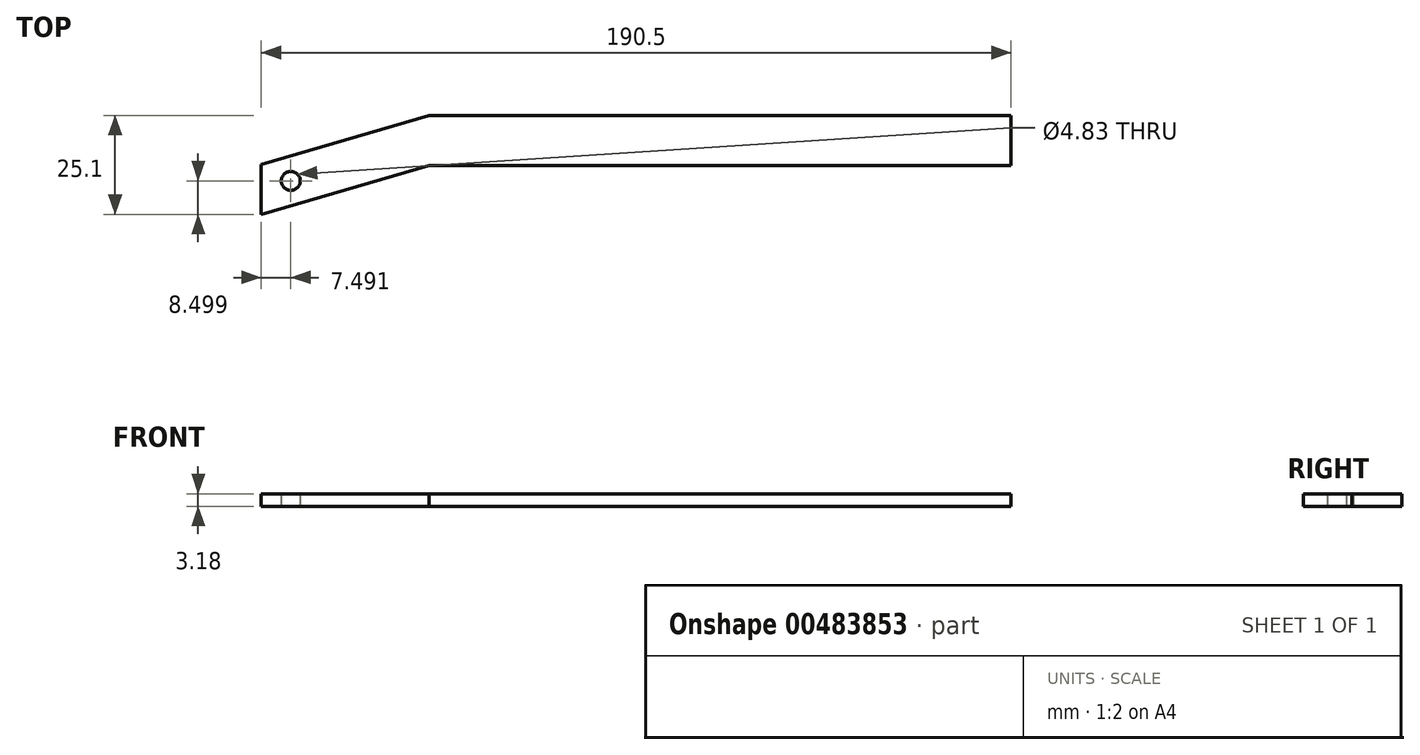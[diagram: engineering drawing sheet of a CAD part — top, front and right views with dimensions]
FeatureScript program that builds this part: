
annotation { "Feature Type Name" : "Feature", "Feature Type Description" : "" }
export const myFeature = defineFeature(function(context is Context, id is Id, definition is map)
    precondition{}
    {
        {
            var Q0;
            Q0=qCreatedBy(makeId("Top.planeOp"),FACE);
            var sketch = newSketch(context, id + "F0", { "sketchPlane" : qUnion([Q0])});
            skLineSegment(sketch, "E0", {"start": v(-47.56, -31.32) * mm, "end": v(-47.56, -18.62) * mm});
            skLineSegment(sketch, "E1", {"start": v(-47.56, -31.32) * mm, "end": v(-4.88, -18.92) * mm});
            skLineSegment(sketch, "E2", {"start": v(-47.56, -18.62) * mm, "end": v(-4.88, -6.22) * mm});
            skLineSegment(sketch, "E3", {"start": v(-4.88, -18.92) * mm, "end": v(79.44, -18.92) * mm});
            skLineSegment(sketch, "E4.bottom", {"start": v(79.44, -18.92) * mm, "end": v(92.14, -18.92) * mm});
            skLineSegment(sketch, "E5", {"start": v(92.14, -18.92) * mm, "end": v(142.94, -18.92) * mm});
            skLineSegment(sketch, "E6", {"start": v(142.94, -18.92) * mm, "end": v(142.94, -6.22) * mm});
            skLineSegment(sketch, "E7", {"start": v(-4.88, -6.22) * mm, "end": v(142.94, -6.22) * mm});
            skCircle(sketch, "E8", {"center": v(-40.07, -22.82) * mm, "radius": 2.41 * mm});
            skSolve(sketch);
        }
        {
            var Q0;
            Q0=qSketchRegion(id+"F0",true);
            extrude(context, id + "F1", {"entities" : qUnion([Q0]), "depth" : 3.17 * mm});
        }
    });
